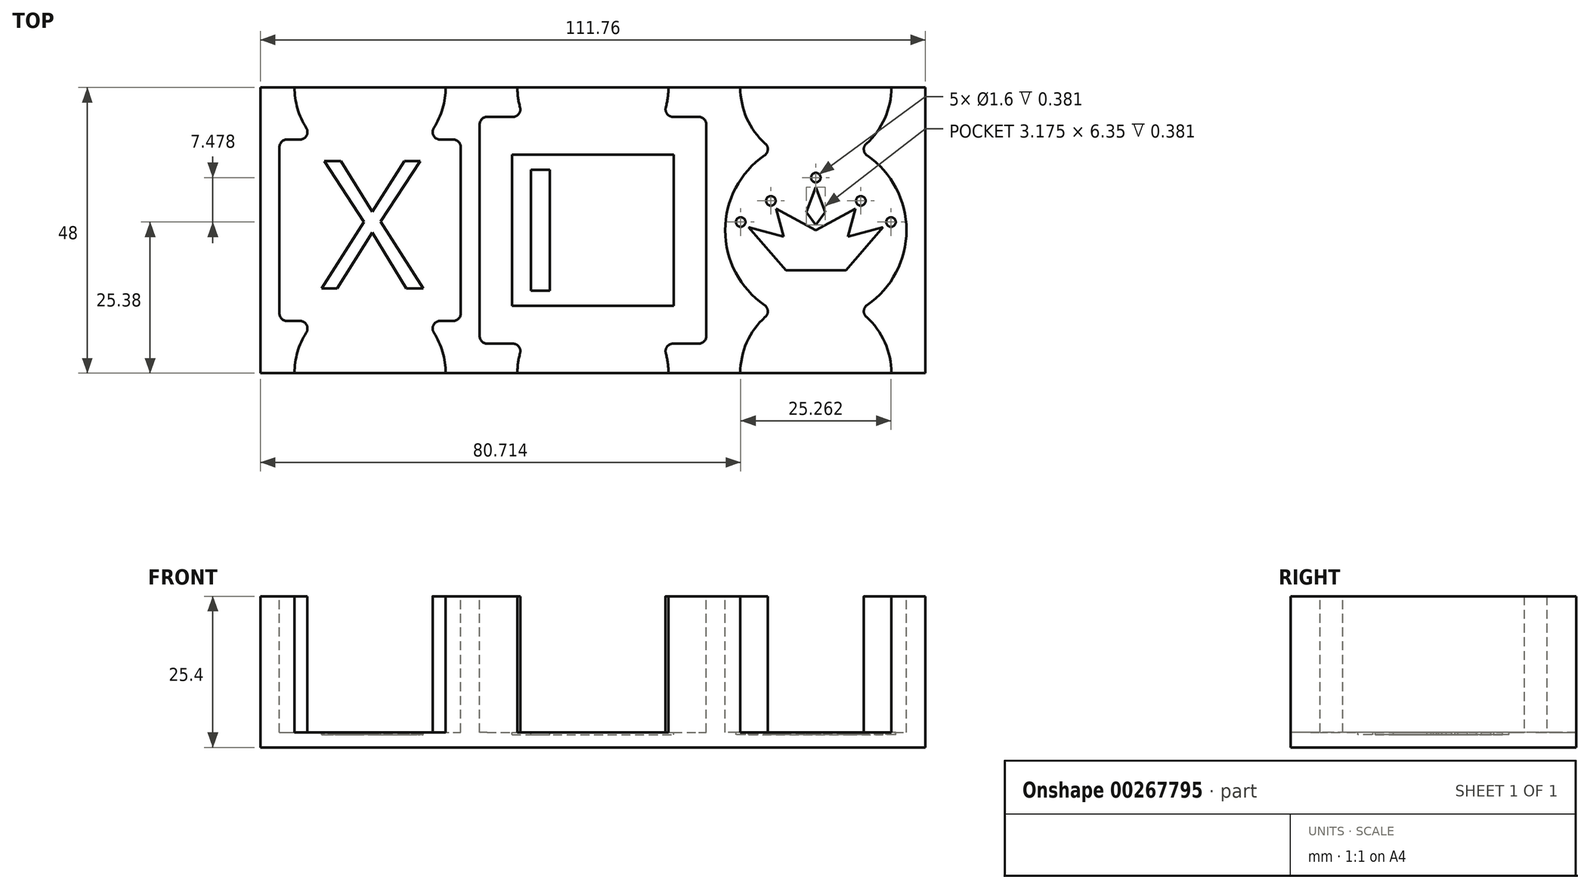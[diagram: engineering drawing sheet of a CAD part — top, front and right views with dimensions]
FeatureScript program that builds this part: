
annotation { "Feature Type Name" : "Feature", "Feature Type Description" : "" }
export const myFeature = defineFeature(function(context is Context, id is Id, definition is map)
    precondition{}
    {
        {
            var Q0;
            Q0=qCreatedBy(makeId("Top.planeOp"),FACE);
            var sketch = newSketch(context, id + "F0", { "sketchPlane" : qUnion([Q0])});
            skLineSegment(sketch, "E0.bottom", {"start": v(0, 0) * mm, "end": v(111.76, 0) * mm});
            skLineSegment(sketch, "E0.top", {"start": v(0, 48) * mm, "end": v(111.76, 48) * mm});
            skLineSegment(sketch, "E0.left", {"start": v(0, 0) * mm, "end": v(0, 48) * mm});
            skLineSegment(sketch, "E0.right", {"start": v(111.76, 0) * mm, "end": v(111.76, 48) * mm});
            skSolve(sketch);
        }
        {
            var Q0;
            Q0 = qSketchRegion(id + "F0", true);
            var Q1;
            Q1=makeQuery(id+"F0.imprint","IMPRINT",FACE,{"disambiguationData":[TD([[makeQuery(id+"F0.imprint","IMPRINT",EDGE,{"derivedFrom":sQuery(id+"F0.wireOp",EDGE,"E0.bottom")}),1.0]])]});
            extrude(context, id + "F1", {"entities" : qUnion([Q0, Q1]), "depth" : 25.4 * mm});
        }
        {
            var Q0;
            Q0=makeQuery(id+"F1.opExtrude","CAP_FACE",FACE,{"disambiguationData":[OSD([sQuery(id+"F0.wireOp",EDGE,"E0.bottom"),sQuery(id+"F0.wireOp",EDGE,"E0.top"),sQuery(id+"F0.wireOp",EDGE,"E0.left"),sQuery(id+"F0.wireOp",EDGE,"E0.right")])],"isStart":false});
            var sketch = newSketch(context, id + "F2", { "sketchPlane" : qUnion([Q0])});
            skLineSegment(sketch, "E1.bottom", {"start": v(3.17, 39.24) * mm, "end": v(33.66, 39.24) * mm});
            skLineSegment(sketch, "E1.top", {"start": v(3.18, 8.76) * mm, "end": v(33.66, 8.76) * mm});
            skLineSegment(sketch, "E1.left", {"start": v(3.18, 39.24) * mm, "end": v(3.18, 8.76) * mm});
            skLineSegment(sketch, "E1.right", {"start": v(33.66, 39.24) * mm, "end": v(33.66, 8.76) * mm});
            skLineSegment(sketch, "E2", {"start": v(0, 24) * mm, "end": v(111.76, 24) * mm, "construction": true});
            skLineSegment(sketch, "E3.bottom", {"start": v(36.83, 43.05) * mm, "end": v(74.93, 43.05) * mm});
            skLineSegment(sketch, "E3.top", {"start": v(36.83, 4.95) * mm, "end": v(74.93, 4.95) * mm});
            skLineSegment(sketch, "E3.left", {"start": v(36.83, 43.05) * mm, "end": v(36.83, 4.95) * mm});
            skLineSegment(sketch, "E3.right", {"start": v(74.93, 43.05) * mm, "end": v(74.93, 4.95) * mm});
            skCircle(sketch, "E4", {"center": v(93.34, 24) * mm, "radius": 15.24 * mm});
            skLineSegment(sketch, "E5", {"start": v(18.41, 48) * mm, "end": v(18.41, 0) * mm, "construction": true});
            skPoint(sketch, "E5.startSnap0", {"position": v(18.41, 39.24) * mm});
            skLineSegment(sketch, "E6", {"start": v(52.07, 48) * mm, "end": v(52.07, 0) * mm, "construction": true});
            skPoint(sketch, "E6.startSnap0", {"position": v(52.07, 37.74) * mm});
            skLineSegment(sketch, "E7", {"start": v(55.88, 48) * mm, "end": v(55.88, 0) * mm, "construction": true});
            skPoint(sketch, "E7.startSnap0", {"position": v(55.88, 43.05) * mm});
            skLineSegment(sketch, "E8", {"start": v(93.35, 48) * mm, "end": v(93.35, 0) * mm, "construction": true});
            skCircle(sketch, "E9", {"center": v(18.41, 48) * mm, "radius": 12.7 * mm});
            skCircle(sketch, "E10", {"center": v(18.41, 0) * mm, "radius": 12.7 * mm});
            skCircle(sketch, "E11", {"center": v(55.88, 0) * mm, "radius": 12.7 * mm});
            skCircle(sketch, "E12", {"center": v(93.34, 0) * mm, "radius": 12.7 * mm});
            skCircle(sketch, "E13", {"center": v(93.35, 48) * mm, "radius": 12.7 * mm});
            skCircle(sketch, "E14", {"center": v(55.88, 48) * mm, "radius": 12.7 * mm});
            skSolve(sketch);
        }
        {
            var Q0;
            {var subQ0=sQuery(id+"F2.wireOp",EDGE,"E10");var subQ1=sQuery(id+"F2.wireOp",EDGE,"E1.top");var subQ2=makeQuery(id+"F2.imprint","INTERSECT",VERTEX,{"disambiguationData":[OD(0.0)],"derivedFrom":[subQ1,subQ0]});Q0=makeQuery(id+"F2.imprint","IMPRINT",FACE,{"disambiguationData":[TD([[makeQuery(id+"F2.imprint","IMPRINT",EDGE,{"disambiguationData":[TD([[subQ2,-1.0]])],"derivedFrom":subQ1}),1.0]])]});}
            var Q1;
            {var subQ0=sQuery(id+"F2.wireOp",EDGE,"E10");var subQ1=sQuery(id+"F2.wireOp",EDGE,"E1.top");var subQ2=makeQuery(id+"F2.imprint","INTERSECT",VERTEX,{"disambiguationData":[OD(0.0)],"derivedFrom":[subQ1,subQ0]});Q1=makeQuery(id+"F2.imprint","IMPRINT",FACE,{"disambiguationData":[TD([[makeQuery(id+"F2.imprint","IMPRINT",EDGE,{"disambiguationData":[TD([[subQ2,-1.0]])],"derivedFrom":subQ1}),-1.0]])]});}
            var Q2;
            {var subQ8=sQuery(id+"F2.wireOp",EDGE,"E1.left");Q2=makeQuery(id+"F2.imprint","IMPRINT",FACE,{"disambiguationData":[TD([[makeQuery(id+"F2.imprint","IMPRINT",EDGE,{"derivedFrom":subQ8}),1.0]])]});}
            var Q3;
            {var subQ0=sQuery(id+"F2.wireOp",EDGE,"E9");var subQ1=sQuery(id+"F2.wireOp",EDGE,"E1.bottom");var subQ2=makeQuery(id+"F2.imprint","INTERSECT",VERTEX,{"disambiguationData":[OD(0.0)],"derivedFrom":[subQ1,subQ0]});Q3=makeQuery(id+"F2.imprint","IMPRINT",FACE,{"disambiguationData":[TD([[makeQuery(id+"F2.imprint","IMPRINT",EDGE,{"disambiguationData":[TD([[subQ2,-1.0]])],"derivedFrom":subQ1}),-1.0]])]});}
            var Q4;
            {var subQ0=sQuery(id+"F2.wireOp",EDGE,"E9");var subQ1=sQuery(id+"F2.wireOp",EDGE,"E1.bottom");var subQ2=makeQuery(id+"F2.imprint","INTERSECT",VERTEX,{"disambiguationData":[OD(0.0)],"derivedFrom":[subQ1,subQ0]});Q4=makeQuery(id+"F2.imprint","IMPRINT",FACE,{"disambiguationData":[TD([[makeQuery(id+"F2.imprint","IMPRINT",EDGE,{"disambiguationData":[TD([[subQ2,-1.0]])],"derivedFrom":subQ1}),1.0]])]});}
            var Q5;
            {var subQ0=sQuery(id+"F2.wireOp",EDGE,"6VNJlFrN-HsLR-yqtk-zgC1-PzaJ0Qko1qQN");var subQ1=sQuery(id+"F2.wireOp",EDGE,"PytdOP70-8Pcy-pkTX-zrFx-fBMRvBaB9JIU.bottom");var subQ2=makeQuery(id+"F2.imprint","INTERSECT",VERTEX,{"disambiguationData":[OD(0.0)],"derivedFrom":[subQ1,subQ0]});Q5=makeQuery(id+"F2.imprint","IMPRINT",FACE,{"disambiguationData":[TD([[makeQuery(id+"F2.imprint","IMPRINT",EDGE,{"disambiguationData":[TD([[subQ2,-1.0]])],"derivedFrom":subQ1}),1.0]])]});}
            var Q6;
            {var subQ0=sQuery(id+"F2.wireOp",EDGE,"6VNJlFrN-HsLR-yqtk-zgC1-PzaJ0Qko1qQN");var subQ1=sQuery(id+"F2.wireOp",EDGE,"PytdOP70-8Pcy-pkTX-zrFx-fBMRvBaB9JIU.bottom");var subQ2=makeQuery(id+"F2.imprint","INTERSECT",VERTEX,{"disambiguationData":[OD(0.0)],"derivedFrom":[subQ1,subQ0]});Q6=makeQuery(id+"F2.imprint","IMPRINT",FACE,{"disambiguationData":[TD([[makeQuery(id+"F2.imprint","IMPRINT",EDGE,{"disambiguationData":[TD([[subQ2,-1.0]])],"derivedFrom":subQ1}),-1.0]])]});}
            var Q7;
            {var subQ4=sQuery(id+"F2.wireOp",EDGE,"PytdOP70-8Pcy-pkTX-zrFx-fBMRvBaB9JIU.left");Q7=makeQuery(id+"F2.imprint","IMPRINT",FACE,{"disambiguationData":[TD([[makeQuery(id+"F2.imprint","IMPRINT",EDGE,{"derivedFrom":subQ4}),1.0]])]});}
            var Q8;
            {var subQ0=sQuery(id+"F2.wireOp",EDGE,"zcWIym07-OYqa-bXhW-Vl75-eQe8IS7MttkU");var subQ1=sQuery(id+"F2.wireOp",EDGE,"PytdOP70-8Pcy-pkTX-zrFx-fBMRvBaB9JIU.top");var subQ2=makeQuery(id+"F2.imprint","INTERSECT",VERTEX,{"disambiguationData":[OD(0.0)],"derivedFrom":[subQ1,subQ0]});Q8=makeQuery(id+"F2.imprint","IMPRINT",FACE,{"disambiguationData":[TD([[makeQuery(id+"F2.imprint","IMPRINT",EDGE,{"disambiguationData":[TD([[subQ2,-1.0]])],"derivedFrom":subQ1}),1.0]])]});}
            var Q9;
            {var subQ0=sQuery(id+"F2.wireOp",EDGE,"zcWIym07-OYqa-bXhW-Vl75-eQe8IS7MttkU");var subQ1=sQuery(id+"F2.wireOp",EDGE,"PytdOP70-8Pcy-pkTX-zrFx-fBMRvBaB9JIU.top");var subQ2=makeQuery(id+"F2.imprint","INTERSECT",VERTEX,{"disambiguationData":[OD(0.0)],"derivedFrom":[subQ1,subQ0]});Q9=makeQuery(id+"F2.imprint","IMPRINT",FACE,{"disambiguationData":[TD([[makeQuery(id+"F2.imprint","IMPRINT",EDGE,{"disambiguationData":[TD([[subQ2,-1.0]])],"derivedFrom":subQ1}),-1.0]])]});}
            var Q10;
            {var subQ0=sQuery(id+"F2.wireOp",EDGE,"E11");var subQ1=sQuery(id+"F2.wireOp",EDGE,"E3.top");var subQ2=makeQuery(id+"F2.imprint","INTERSECT",VERTEX,{"disambiguationData":[OD(0.0)],"derivedFrom":[subQ1,subQ0]});Q10=makeQuery(id+"F2.imprint","IMPRINT",FACE,{"disambiguationData":[TD([[makeQuery(id+"F2.imprint","IMPRINT",EDGE,{"disambiguationData":[TD([[subQ2,-1.0]])],"derivedFrom":subQ1}),-1.0]])]});}
            var Q11;
            {var subQ0=sQuery(id+"F2.wireOp",EDGE,"E11");var subQ1=sQuery(id+"F2.wireOp",EDGE,"E3.top");var subQ2=makeQuery(id+"F2.imprint","INTERSECT",VERTEX,{"disambiguationData":[OD(0.0)],"derivedFrom":[subQ1,subQ0]});Q11=makeQuery(id+"F2.imprint","IMPRINT",FACE,{"disambiguationData":[TD([[makeQuery(id+"F2.imprint","IMPRINT",EDGE,{"disambiguationData":[TD([[subQ2,-1.0]])],"derivedFrom":subQ1}),1.0]])]});}
            var Q12;
            {var subQ9=sQuery(id+"F2.wireOp",EDGE,"E3.left");Q12=makeQuery(id+"F2.imprint","IMPRINT",FACE,{"disambiguationData":[TD([[makeQuery(id+"F2.imprint","IMPRINT",EDGE,{"derivedFrom":subQ9}),1.0]])]});}
            var Q13;
            {var subQ0=sQuery(id+"F2.wireOp",EDGE,"E14");var subQ1=sQuery(id+"F2.wireOp",EDGE,"E3.bottom");var subQ2=makeQuery(id+"F2.imprint","INTERSECT",VERTEX,{"disambiguationData":[OD(0.0)],"derivedFrom":[subQ1,subQ0]});Q13=makeQuery(id+"F2.imprint","IMPRINT",FACE,{"disambiguationData":[TD([[makeQuery(id+"F2.imprint","IMPRINT",EDGE,{"disambiguationData":[TD([[subQ2,-1.0]])],"derivedFrom":subQ1}),-1.0]])]});}
            var Q14;
            {var subQ0=sQuery(id+"F2.wireOp",EDGE,"E14");var subQ1=sQuery(id+"F2.wireOp",EDGE,"E3.bottom");var subQ2=makeQuery(id+"F2.imprint","INTERSECT",VERTEX,{"disambiguationData":[OD(0.0)],"derivedFrom":[subQ1,subQ0]});Q14=makeQuery(id+"F2.imprint","IMPRINT",FACE,{"disambiguationData":[TD([[makeQuery(id+"F2.imprint","IMPRINT",EDGE,{"disambiguationData":[TD([[subQ2,-1.0]])],"derivedFrom":subQ1}),1.0]])]});}
            var Q15;
            {var subQ0=sQuery(id+"F2.wireOp",EDGE,"E13");var subQ1=sQuery(id+"F2.wireOp",EDGE,"E4");var subQ2=makeQuery(id+"F2.imprint","INTERSECT",VERTEX,{"disambiguationData":[OD(0.0)],"derivedFrom":[subQ1,subQ0]});Q15=makeQuery(id+"F2.imprint","IMPRINT",FACE,{"disambiguationData":[TD([[makeQuery(id+"F2.imprint","IMPRINT",EDGE,{"disambiguationData":[TD([[subQ2,1.0]])],"derivedFrom":subQ1}),-1.0]])]});}
            var Q16;
            {var subQ0=sQuery(id+"F2.wireOp",EDGE,"E13");var subQ1=sQuery(id+"F2.wireOp",EDGE,"E4");var subQ2=makeQuery(id+"F2.imprint","INTERSECT",VERTEX,{"disambiguationData":[OD(0.0)],"derivedFrom":[subQ1,subQ0]});Q16=makeQuery(id+"F2.imprint","IMPRINT",FACE,{"disambiguationData":[TD([[makeQuery(id+"F2.imprint","IMPRINT",EDGE,{"disambiguationData":[TD([[subQ2,1.0]])],"derivedFrom":subQ1}),1.0]])]});}
            var Q17;
            {var subQ0=sQuery(id+"F2.wireOp",EDGE,"E13");var subQ1=sQuery(id+"F2.wireOp",EDGE,"E4");var subQ2=makeQuery(id+"F2.imprint","INTERSECT",VERTEX,{"disambiguationData":[OD(0.0)],"derivedFrom":[subQ1,subQ0]});Q17=makeQuery(id+"F2.imprint","IMPRINT",FACE,{"disambiguationData":[TD([[makeQuery(id+"F2.imprint","IMPRINT",EDGE,{"disambiguationData":[TD([[subQ2,-1.0]])],"derivedFrom":subQ1}),1.0]])]});}
            var Q18;
            {var subQ0=sQuery(id+"F2.wireOp",EDGE,"E12");var subQ1=sQuery(id+"F2.wireOp",EDGE,"E4");var subQ2=makeQuery(id+"F2.imprint","INTERSECT",VERTEX,{"disambiguationData":[OD(0.0)],"derivedFrom":[subQ1,subQ0]});Q18=makeQuery(id+"F2.imprint","IMPRINT",FACE,{"disambiguationData":[TD([[makeQuery(id+"F2.imprint","IMPRINT",EDGE,{"disambiguationData":[TD([[subQ2,-1.0]])],"derivedFrom":subQ1}),1.0]])]});}
            var Q19;
            {var subQ0=sQuery(id+"F2.wireOp",EDGE,"E12");var subQ1=sQuery(id+"F2.wireOp",EDGE,"E4");var subQ2=makeQuery(id+"F2.imprint","INTERSECT",VERTEX,{"disambiguationData":[OD(0.0)],"derivedFrom":[subQ1,subQ0]});Q19=makeQuery(id+"F2.imprint","IMPRINT",FACE,{"disambiguationData":[TD([[makeQuery(id+"F2.imprint","IMPRINT",EDGE,{"disambiguationData":[TD([[subQ2,-1.0]])],"derivedFrom":subQ1}),-1.0]])]});}
            extrude(context, id + "F3", {"entities" : qUnion([Q0, Q1, Q2, Q3, Q4, Q5, Q6, Q7, Q8, Q9, Q10, Q11, Q12, Q13, Q14, Q15, Q16, Q17, Q18, Q19]), "operationType" : NewBodyOperationType.REMOVE, "oppositeDirection" : true, "depth" : 22.86 * mm});
        }
        {
            var Q0;
            Q0=makeQuery(id+"F3.boolean.opBoolean","COPY",FACE,{"derivedFrom":makeQuery(id+"F3.opExtrude","CAP_FACE",FACE,{"disambiguationData":[OSD([sQuery(id+"F0.wireOp",EDGE,"E0.bottom"),sQuery(id+"F0.wireOp",EDGE,"E0.top"),sQuery(id+"F2.wireOp",EDGE,"E1.bottom"),sQuery(id+"F2.wireOp",EDGE,"E1.top"),sQuery(id+"F2.wireOp",EDGE,"E1.left"),sQuery(id+"F2.wireOp",EDGE,"E1.right"),sQuery(id+"F2.wireOp",EDGE,"E9"),sQuery(id+"F2.wireOp",EDGE,"E10")])],"isStart":false})});
            var sketch = newSketch(context, id + "F4", { "sketchPlane" : qUnion([Q0])});
            skText(sketch, "E15", { "text": "X\n", "fontName": "OpenSans-Regular.ttf"});
            skLineSegment(sketch, "E16", {"start": v(3.18, 24) * mm, "end": v(160.37, 24) * mm, "construction": true});
            skLineSegment(sketch, "E17.bottom", {"start": v(42.28, 36.7) * mm, "end": v(69.48, 36.7) * mm});
            skLineSegment(sketch, "E17.top", {"start": v(42.28, 11.3) * mm, "end": v(69.48, 11.3) * mm});
            skLineSegment(sketch, "E17.left", {"start": v(42.28, 36.7) * mm, "end": v(42.28, 11.3) * mm});
            skLineSegment(sketch, "E17.right", {"start": v(69.48, 36.7) * mm, "end": v(69.48, 11.3) * mm});
            skLineSegment(sketch, "E18.bottom", {"start": v(45.45, 34.16) * mm, "end": v(48.63, 34.16) * mm});
            skLineSegment(sketch, "E18.top", {"start": v(45.45, 13.84) * mm, "end": v(48.63, 13.84) * mm});
            skLineSegment(sketch, "E18.left", {"start": v(45.45, 34.16) * mm, "end": v(45.45, 13.84) * mm});
            skLineSegment(sketch, "E18.right", {"start": v(48.63, 34.16) * mm, "end": v(48.63, 13.84) * mm});
            skLineSegment(sketch, "E19", {"start": v(88.3, 17.3) * mm, "end": v(82.06, 24.52) * mm});
            skLineSegment(sketch, "E20", {"start": v(82.06, 24.52) * mm, "end": v(87.93, 22.92) * mm});
            skLineSegment(sketch, "E21", {"start": v(87.93, 22.92) * mm, "end": v(86.66, 27.6) * mm});
            skLineSegment(sketch, "E22", {"start": v(86.66, 27.6) * mm, "end": v(93.35, 24.02) * mm});
            skLineSegment(sketch, "E23", {"start": v(93.35, 24.02) * mm, "end": v(100.03, 27.6) * mm});
            skLineSegment(sketch, "E24", {"start": v(100.03, 27.6) * mm, "end": v(98.76, 22.92) * mm});
            skLineSegment(sketch, "E25", {"start": v(98.76, 22.92) * mm, "end": v(104.63, 24.52) * mm});
            skLineSegment(sketch, "E26", {"start": v(104.63, 24.52) * mm, "end": v(98.4, 17.3) * mm});
            skLineSegment(sketch, "E27", {"start": v(98.4, 17.3) * mm, "end": v(88.3, 17.3) * mm});
            skLineSegment(sketch, "E28", {"start": v(93.35, 9.8) * mm, "end": v(93.35, 43) * mm, "construction": true});
            skPoint(sketch, "E28.startSnap0", {"position": v(93.35, 17.3) * mm});
            skLineSegment(sketch, "E29", {"start": v(91.76, 27.06) * mm, "end": v(93.35, 24.9) * mm});
            skLineSegment(sketch, "E30", {"start": v(93.35, 24.9) * mm, "end": v(94.93, 27.06) * mm});
            skLineSegment(sketch, "E31", {"start": v(94.93, 27.06) * mm, "end": v(93.35, 31.26) * mm});
            skLineSegment(sketch, "E32", {"start": v(93.35, 31.26) * mm, "end": v(91.76, 27.06) * mm});
            skLineSegment(sketch, "E33", {"start": v(93.35, 17.3) * mm, "end": v(82.06, 24.52) * mm, "construction": true});
            skLineSegment(sketch, "E34", {"start": v(82.06, 24.52) * mm, "end": v(80.71, 25.38) * mm, "construction": true});
            skLineSegment(sketch, "E35", {"start": v(86.66, 27.6) * mm, "end": v(93.35, 17.3) * mm, "construction": true});
            skLineSegment(sketch, "E36", {"start": v(86.66, 27.6) * mm, "end": v(85.79, 28.95) * mm, "construction": true});
            skLineSegment(sketch, "E37", {"start": v(93.35, 17.3) * mm, "end": v(100.03, 27.6) * mm, "construction": true});
            skLineSegment(sketch, "E38", {"start": v(100.03, 27.6) * mm, "end": v(100.9, 28.95) * mm, "construction": true});
            skLineSegment(sketch, "E39", {"start": v(93.35, 17.3) * mm, "end": v(104.63, 24.52) * mm, "construction": true});
            skLineSegment(sketch, "E40", {"start": v(104.63, 24.52) * mm, "end": v(105.98, 25.38) * mm, "construction": true});
            skCircle(sketch, "E41", {"center": v(80.71, 25.38) * mm, "radius": 0.8 * mm});
            skCircle(sketch, "E42", {"center": v(85.79, 28.95) * mm, "radius": 0.8 * mm});
            skCircle(sketch, "E43", {"center": v(93.35, 32.86) * mm, "radius": 0.8 * mm});
            skCircle(sketch, "E44", {"center": v(100.9, 28.95) * mm, "radius": 0.8 * mm});
            skCircle(sketch, "E45", {"center": v(105.98, 25.38) * mm, "radius": 0.8 * mm});
            skLineSegment(sketch, "E46", {"start": v(55.88, 45.3) * mm, "end": v(55.88, 7.15) * mm, "construction": true});
            skPoint(sketch, "E46.startSnap0", {"position": v(55.88, 36.7) * mm});
            const initialGuessF4  = {"E15": [0.01015, 0.0142, 1, 0, 0.02159]};
            skSetInitialGuess(sketch, initialGuessF4);
            skSolve(sketch);
        }
        {
            var Q0;
            Q0=makeQuery(id+"F4.imprint","IMPRINT",FACE,{"disambiguationData":[TD([[makeQuery(id+"F4.imprint","IMPRINT",EDGE,{"derivedFrom":sQuery(id+"F4.wireOp",EDGE,"E15.sketch_text.stroke-0")}),-1.0]])]});
            var Q1;
            Q1=makeQuery(id+"F4.imprint","IMPRINT",FACE,{"disambiguationData":[TD([[makeQuery(id+"F4.imprint","IMPRINT",EDGE,{"derivedFrom":sQuery(id+"F4.wireOp",EDGE,"2d5831eb-de9d-4b13-afd4-8ee156c4e702.sketch_text.stroke-0")}),-1.0]])]});
            var Q2;
            Q2=makeQuery(id+"F4.imprint","IMPRINT",FACE,{"disambiguationData":[TD([[makeQuery(id+"F4.imprint","IMPRINT",EDGE,{"derivedFrom":sQuery(id+"F4.wireOp",EDGE,"E17.bottom")}),-1.0]])]});
            var Q3;
            Q3=makeQuery(id+"F4.imprint","IMPRINT",FACE,{"disambiguationData":[TD([[makeQuery(id+"F4.imprint","IMPRINT",EDGE,{"derivedFrom":sQuery(id+"F4.wireOp",EDGE,"E19")}),-1.0]])]});
            var Q4;
            Q4=makeQuery(id+"F4.imprint","IMPRINT",FACE,{"disambiguationData":[TD([[makeQuery(id+"F4.imprint","IMPRINT",EDGE,{"derivedFrom":sQuery(id+"F4.wireOp",EDGE,"E42")}),1.0]])]});
            var Q5;
            Q5=makeQuery(id+"F4.imprint","IMPRINT",FACE,{"disambiguationData":[TD([[makeQuery(id+"F4.imprint","IMPRINT",EDGE,{"derivedFrom":sQuery(id+"F4.wireOp",EDGE,"E41")}),1.0]])]});
            var Q6;
            Q6=makeQuery(id+"F4.imprint","IMPRINT",FACE,{"disambiguationData":[TD([[makeQuery(id+"F4.imprint","IMPRINT",EDGE,{"derivedFrom":sQuery(id+"F4.wireOp",EDGE,"E29")}),1.0]])]});
            var Q7;
            Q7=makeQuery(id+"F4.imprint","IMPRINT",FACE,{"disambiguationData":[TD([[makeQuery(id+"F4.imprint","IMPRINT",EDGE,{"derivedFrom":sQuery(id+"F4.wireOp",EDGE,"E43")}),1.0]])]});
            var Q8;
            Q8=makeQuery(id+"F4.imprint","IMPRINT",FACE,{"disambiguationData":[TD([[makeQuery(id+"F4.imprint","IMPRINT",EDGE,{"derivedFrom":sQuery(id+"F4.wireOp",EDGE,"E44")}),1.0]])]});
            var Q9;
            Q9=makeQuery(id+"F4.imprint","IMPRINT",FACE,{"disambiguationData":[TD([[makeQuery(id+"F4.imprint","IMPRINT",EDGE,{"derivedFrom":sQuery(id+"F4.wireOp",EDGE,"E45")}),1.0]])]});
            extrude(context, id + "F5", {"entities" : qUnion([Q0, Q1, Q2, Q3, Q4, Q5, Q6, Q7, Q8, Q9]), "operationType" : NewBodyOperationType.REMOVE, "oppositeDirection" : true, "depth" : 0.38 * mm});
        }
        {
            var Q0;
            Q0=makeQuery(id+"F3.boolean.opBoolean","COPY",EDGE,{"derivedFrom":makeQuery(id+"F3.opExtrude","SWEPT_EDGE",EDGE,{"disambiguationData":[OSD([sQuery(id+"F2.wireOp",EDGE,"E1.bottom"),sQuery(id+"F2.wireOp",EDGE,"E1.right")])]})});
            var Q1;
            Q1=makeQuery(id+"F3.boolean.opBoolean","COPY",EDGE,{"derivedFrom":makeQuery(id+"F3.opExtrude","SWEPT_EDGE",EDGE,{"disambiguationData":[OSD([sQuery(id+"F2.wireOp",EDGE,"E1.bottom"),sQuery(id+"F2.wireOp",EDGE,"E1.left")])]})});
            var Q2;
            Q2=makeQuery(id+"F3.boolean.opBoolean","COPY",EDGE,{"derivedFrom":makeQuery(id+"F3.opExtrude","SWEPT_EDGE",EDGE,{"disambiguationData":[OSD([sQuery(id+"F2.wireOp",EDGE,"E1.top"),sQuery(id+"F2.wireOp",EDGE,"E1.right")])]})});
            var Q3;
            Q3=makeQuery(id+"F3.boolean.opBoolean","COPY",EDGE,{"derivedFrom":makeQuery(id+"F3.opExtrude","SWEPT_EDGE",EDGE,{"disambiguationData":[OSD([sQuery(id+"F2.wireOp",EDGE,"E1.top"),sQuery(id+"F2.wireOp",EDGE,"E1.left")])]})});
            var Q4;
            Q4=makeQuery(id+"F3.boolean.opBoolean","COPY",EDGE,{"derivedFrom":makeQuery(id+"F3.opExtrude","SWEPT_EDGE",EDGE,{"disambiguationData":[OSD([sQuery(id+"F2.wireOp",EDGE,"PytdOP70-8Pcy-pkTX-zrFx-fBMRvBaB9JIU.top"),sQuery(id+"F2.wireOp",EDGE,"PytdOP70-8Pcy-pkTX-zrFx-fBMRvBaB9JIU.left")])]})});
            var Q5;
            Q5=makeQuery(id+"F3.boolean.opBoolean","COPY",EDGE,{"derivedFrom":makeQuery(id+"F3.opExtrude","SWEPT_EDGE",EDGE,{"disambiguationData":[OSD([sQuery(id+"F2.wireOp",EDGE,"PytdOP70-8Pcy-pkTX-zrFx-fBMRvBaB9JIU.bottom"),sQuery(id+"F2.wireOp",EDGE,"PytdOP70-8Pcy-pkTX-zrFx-fBMRvBaB9JIU.left")])]})});
            var Q6;
            Q6=makeQuery(id+"F3.boolean.opBoolean","COPY",EDGE,{"derivedFrom":makeQuery(id+"F3.opExtrude","SWEPT_EDGE",EDGE,{"disambiguationData":[OSD([sQuery(id+"F2.wireOp",EDGE,"PytdOP70-8Pcy-pkTX-zrFx-fBMRvBaB9JIU.bottom"),sQuery(id+"F2.wireOp",EDGE,"PytdOP70-8Pcy-pkTX-zrFx-fBMRvBaB9JIU.right")])]})});
            var Q7;
            Q7=makeQuery(id+"F3.boolean.opBoolean","COPY",EDGE,{"derivedFrom":makeQuery(id+"F3.opExtrude","SWEPT_EDGE",EDGE,{"disambiguationData":[OSD([sQuery(id+"F2.wireOp",EDGE,"PytdOP70-8Pcy-pkTX-zrFx-fBMRvBaB9JIU.top"),sQuery(id+"F2.wireOp",EDGE,"PytdOP70-8Pcy-pkTX-zrFx-fBMRvBaB9JIU.right")])]})});
            var Q8;
            Q8=makeQuery(id+"F3.boolean.opBoolean","COPY",EDGE,{"derivedFrom":makeQuery(id+"F3.opExtrude","SWEPT_EDGE",EDGE,{"disambiguationData":[OSD([sQuery(id+"F2.wireOp",EDGE,"E3.top"),sQuery(id+"F2.wireOp",EDGE,"E3.left")])]})});
            var Q9;
            Q9=makeQuery(id+"F3.boolean.opBoolean","COPY",EDGE,{"derivedFrom":makeQuery(id+"F3.opExtrude","SWEPT_EDGE",EDGE,{"disambiguationData":[OSD([sQuery(id+"F2.wireOp",EDGE,"E3.bottom"),sQuery(id+"F2.wireOp",EDGE,"E3.left")])]})});
            var Q10;
            Q10=makeQuery(id+"F3.boolean.opBoolean","COPY",EDGE,{"derivedFrom":makeQuery(id+"F3.opExtrude","SWEPT_EDGE",EDGE,{"disambiguationData":[OSD([sQuery(id+"F2.wireOp",EDGE,"E3.bottom"),sQuery(id+"F2.wireOp",EDGE,"E3.right")])]})});
            var Q11;
            Q11=makeQuery(id+"F3.boolean.opBoolean","COPY",EDGE,{"derivedFrom":makeQuery(id+"F3.opExtrude","SWEPT_EDGE",EDGE,{"disambiguationData":[OSD([sQuery(id+"F2.wireOp",EDGE,"E3.top"),sQuery(id+"F2.wireOp",EDGE,"E3.right")])]})});
            var Q12;
            {var subQ0=sQuery(id+"F2.wireOp",EDGE,"E12");var subQ1=sQuery(id+"F2.wireOp",EDGE,"E4");Q12=makeQuery(id+"F3.boolean.opBoolean","COPY",EDGE,{"derivedFrom":makeQuery(id+"F3.opExtrude","SWEPT_EDGE",EDGE,{"disambiguationData":[OSD([subQ1,subQ0]),TDD([makeQuery(id+"F2.imprint","INTERSECT",VERTEX,{"disambiguationData":[OD(0.0)],"derivedFrom":[subQ1,subQ0]})])]})});}
            var Q13;
            {var subQ0=sQuery(id+"F2.wireOp",EDGE,"E12");var subQ1=sQuery(id+"F2.wireOp",EDGE,"E4");Q13=makeQuery(id+"F3.boolean.opBoolean","COPY",EDGE,{"derivedFrom":makeQuery(id+"F3.opExtrude","SWEPT_EDGE",EDGE,{"disambiguationData":[OSD([subQ1,subQ0]),TDD([makeQuery(id+"F2.imprint","INTERSECT",VERTEX,{"disambiguationData":[OD(1.0)],"derivedFrom":[subQ1,subQ0]})])]})});}
            var Q14;
            {var subQ0=sQuery(id+"F2.wireOp",EDGE,"E13");var subQ1=sQuery(id+"F2.wireOp",EDGE,"E4");Q14=makeQuery(id+"F3.boolean.opBoolean","COPY",EDGE,{"derivedFrom":makeQuery(id+"F3.opExtrude","SWEPT_EDGE",EDGE,{"disambiguationData":[OSD([subQ1,subQ0]),TDD([makeQuery(id+"F2.imprint","INTERSECT",VERTEX,{"disambiguationData":[OD(1.0)],"derivedFrom":[subQ1,subQ0]})])]})});}
            var Q15;
            {var subQ0=sQuery(id+"F2.wireOp",EDGE,"E13");var subQ1=sQuery(id+"F2.wireOp",EDGE,"E4");Q15=makeQuery(id+"F3.boolean.opBoolean","COPY",EDGE,{"derivedFrom":makeQuery(id+"F3.opExtrude","SWEPT_EDGE",EDGE,{"disambiguationData":[OSD([subQ1,subQ0]),TDD([makeQuery(id+"F2.imprint","INTERSECT",VERTEX,{"disambiguationData":[OD(0.0)],"derivedFrom":[subQ1,subQ0]})])]})});}
            var Q16;
            {var subQ0=sQuery(id+"F2.wireOp",EDGE,"E11");var subQ1=sQuery(id+"F2.wireOp",EDGE,"E3.top");Q16=makeQuery(id+"F3.boolean.opBoolean","COPY",EDGE,{"derivedFrom":makeQuery(id+"F3.opExtrude","SWEPT_EDGE",EDGE,{"disambiguationData":[OSD([subQ1,subQ0]),TDD([makeQuery(id+"F2.imprint","INTERSECT",VERTEX,{"disambiguationData":[OD(1.0)],"derivedFrom":[subQ1,subQ0]})])]})});}
            var Q17;
            {var subQ0=sQuery(id+"F2.wireOp",EDGE,"E11");var subQ1=sQuery(id+"F2.wireOp",EDGE,"E3.top");Q17=makeQuery(id+"F3.boolean.opBoolean","COPY",EDGE,{"derivedFrom":makeQuery(id+"F3.opExtrude","SWEPT_EDGE",EDGE,{"disambiguationData":[OSD([subQ1,subQ0]),TDD([makeQuery(id+"F2.imprint","INTERSECT",VERTEX,{"disambiguationData":[OD(0.0)],"derivedFrom":[subQ1,subQ0]})])]})});}
            var Q18;
            {var subQ0=sQuery(id+"F2.wireOp",EDGE,"E14");var subQ1=sQuery(id+"F2.wireOp",EDGE,"E3.bottom");Q18=makeQuery(id+"F3.boolean.opBoolean","COPY",EDGE,{"derivedFrom":makeQuery(id+"F3.opExtrude","SWEPT_EDGE",EDGE,{"disambiguationData":[OSD([subQ1,subQ0]),TDD([makeQuery(id+"F2.imprint","INTERSECT",VERTEX,{"disambiguationData":[OD(0.0)],"derivedFrom":[subQ1,subQ0]})])]})});}
            var Q19;
            {var subQ0=sQuery(id+"F2.wireOp",EDGE,"E14");var subQ1=sQuery(id+"F2.wireOp",EDGE,"E3.bottom");Q19=makeQuery(id+"F3.boolean.opBoolean","COPY",EDGE,{"derivedFrom":makeQuery(id+"F3.opExtrude","SWEPT_EDGE",EDGE,{"disambiguationData":[OSD([subQ1,subQ0]),TDD([makeQuery(id+"F2.imprint","INTERSECT",VERTEX,{"disambiguationData":[OD(1.0)],"derivedFrom":[subQ1,subQ0]})])]})});}
            var Q20;
            {var subQ0=sQuery(id+"F2.wireOp",EDGE,"E9");var subQ1=sQuery(id+"F2.wireOp",EDGE,"E1.bottom");Q20=makeQuery(id+"F3.boolean.opBoolean","COPY",EDGE,{"derivedFrom":makeQuery(id+"F3.opExtrude","SWEPT_EDGE",EDGE,{"disambiguationData":[OSD([subQ1,subQ0]),TDD([makeQuery(id+"F2.imprint","INTERSECT",VERTEX,{"disambiguationData":[OD(0.0)],"derivedFrom":[subQ1,subQ0]})])]})});}
            var Q21;
            {var subQ0=sQuery(id+"F2.wireOp",EDGE,"E9");var subQ1=sQuery(id+"F2.wireOp",EDGE,"E1.bottom");Q21=makeQuery(id+"F3.boolean.opBoolean","COPY",EDGE,{"derivedFrom":makeQuery(id+"F3.opExtrude","SWEPT_EDGE",EDGE,{"disambiguationData":[OSD([subQ1,subQ0]),TDD([makeQuery(id+"F2.imprint","INTERSECT",VERTEX,{"disambiguationData":[OD(1.0)],"derivedFrom":[subQ1,subQ0]})])]})});}
            var Q22;
            {var subQ0=sQuery(id+"F2.wireOp",EDGE,"E10");var subQ1=sQuery(id+"F2.wireOp",EDGE,"E1.top");Q22=makeQuery(id+"F3.boolean.opBoolean","COPY",EDGE,{"derivedFrom":makeQuery(id+"F3.opExtrude","SWEPT_EDGE",EDGE,{"disambiguationData":[OSD([subQ1,subQ0]),TDD([makeQuery(id+"F2.imprint","INTERSECT",VERTEX,{"disambiguationData":[OD(0.0)],"derivedFrom":[subQ1,subQ0]})])]})});}
            var Q23;
            {var subQ0=sQuery(id+"F2.wireOp",EDGE,"E10");var subQ1=sQuery(id+"F2.wireOp",EDGE,"E1.top");Q23=makeQuery(id+"F3.boolean.opBoolean","COPY",EDGE,{"derivedFrom":makeQuery(id+"F3.opExtrude","SWEPT_EDGE",EDGE,{"disambiguationData":[OSD([subQ1,subQ0]),TDD([makeQuery(id+"F2.imprint","INTERSECT",VERTEX,{"disambiguationData":[OD(1.0)],"derivedFrom":[subQ1,subQ0]})])]})});}
            var Q24;
            {var subQ0=sQuery(id+"F2.wireOp",EDGE,"zcWIym07-OYqa-bXhW-Vl75-eQe8IS7MttkU");var subQ1=sQuery(id+"F2.wireOp",EDGE,"PytdOP70-8Pcy-pkTX-zrFx-fBMRvBaB9JIU.top");Q24=makeQuery(id+"F3.boolean.opBoolean","COPY",EDGE,{"derivedFrom":makeQuery(id+"F3.opExtrude","SWEPT_EDGE",EDGE,{"disambiguationData":[OSD([subQ1,subQ0]),TDD([makeQuery(id+"F2.imprint","INTERSECT",VERTEX,{"disambiguationData":[OD(0.0)],"derivedFrom":[subQ1,subQ0]})])]})});}
            var Q25;
            {var subQ0=sQuery(id+"F2.wireOp",EDGE,"zcWIym07-OYqa-bXhW-Vl75-eQe8IS7MttkU");var subQ1=sQuery(id+"F2.wireOp",EDGE,"PytdOP70-8Pcy-pkTX-zrFx-fBMRvBaB9JIU.top");Q25=makeQuery(id+"F3.boolean.opBoolean","COPY",EDGE,{"derivedFrom":makeQuery(id+"F3.opExtrude","SWEPT_EDGE",EDGE,{"disambiguationData":[OSD([subQ1,subQ0]),TDD([makeQuery(id+"F2.imprint","INTERSECT",VERTEX,{"disambiguationData":[OD(1.0)],"derivedFrom":[subQ1,subQ0]})])]})});}
            var Q26;
            {var subQ0=sQuery(id+"F2.wireOp",EDGE,"6VNJlFrN-HsLR-yqtk-zgC1-PzaJ0Qko1qQN");var subQ1=sQuery(id+"F2.wireOp",EDGE,"PytdOP70-8Pcy-pkTX-zrFx-fBMRvBaB9JIU.bottom");Q26=makeQuery(id+"F3.boolean.opBoolean","COPY",EDGE,{"derivedFrom":makeQuery(id+"F3.opExtrude","SWEPT_EDGE",EDGE,{"disambiguationData":[OSD([subQ1,subQ0]),TDD([makeQuery(id+"F2.imprint","INTERSECT",VERTEX,{"disambiguationData":[OD(0.0)],"derivedFrom":[subQ1,subQ0]})])]})});}
            var Q27;
            {var subQ0=sQuery(id+"F2.wireOp",EDGE,"6VNJlFrN-HsLR-yqtk-zgC1-PzaJ0Qko1qQN");var subQ1=sQuery(id+"F2.wireOp",EDGE,"PytdOP70-8Pcy-pkTX-zrFx-fBMRvBaB9JIU.bottom");Q27=makeQuery(id+"F3.boolean.opBoolean","COPY",EDGE,{"derivedFrom":makeQuery(id+"F3.opExtrude","SWEPT_EDGE",EDGE,{"disambiguationData":[OSD([subQ1,subQ0]),TDD([makeQuery(id+"F2.imprint","INTERSECT",VERTEX,{"disambiguationData":[OD(1.0)],"derivedFrom":[subQ1,subQ0]})])]})});}
            fillet(context, id + "F6", {"entities" : qUnion([Q0, Q1, Q2, Q3, Q4, Q5, Q6, Q7, Q8, Q9, Q10, Q11, Q12, Q13, Q14, Q15, Q16, Q17, Q18, Q19, Q20, Q21, Q22, Q23, Q24, Q25, Q26, Q27]), "radius" : 1.27 * mm, "tangentPropagation" : true, "allowEdgeOverflow" : false});
        }
    });
